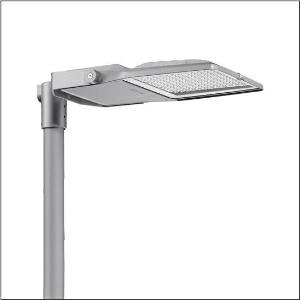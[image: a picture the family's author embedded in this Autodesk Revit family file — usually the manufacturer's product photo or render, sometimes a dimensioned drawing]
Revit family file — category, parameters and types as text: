
# Revit family: floodlight_fl_21_iq_midi___pl33t_5xa7782f4f3a_5715
name_source: partatom
category: Lighting Fixtures
units: mm (PartAtom-declared; Revit-internal decimal feet)

## family parameters
Cut with Voids When Loaded = No
Host = Face
Light Source = No
Part Type = Normal
Room Calculation Point = No
Round Connector Dimension = Use Diameter
Shared = No

## types (1)
- --- (1 x LED, 36900 lm, 270.2 W, 4000K)
    Apparent Load = 270 VA
    CIE Flux Codes = 26 75 99 100 100
    Color Rendering = 70
    Color Temperature = 4000K
    Default Elevation = 1800 mm
    Description = Floodlight FL 21 iQ midi, floodlight, primary light control with lens, of PMMA, primary optical cover: protective disc, of toughened safety glass, transparent, light distribution: PL33T, light emission: direct distribution, installation type: surface-mounted, LED, High Power LED, rated luminous flux: 36.900lm, luminous efficacy: 137lm/W, light colour: 740, colour temperature: 4000K, control gear: ECG iQ, control: optimised constant luminous flux control (CLO 2.0), Desk-Remote (wireless, voltage-free reading and setting of iQ features in the workshop via application-optimized NFC function/RFID function), Smart-Wire, Night-Set, Temp-Guard, Auto-Match, Street-Remote, with terminal, 6-pole, mains connection: 220..240V, AC, 50/60Hz, start of lifetime: 270W, end of service life: 287W, reduction: 118W, luminaire housing, of diecast aluminium, powder-coated, Siteco® metallic grey (DB 702S), corrosivity category C5 mid according to DIN EN ISO 12944, sealing non-destructively replaceable, please order mast flange separately, mast bracket, of steel, galvanised, powder-coated, Siteco® metallic grey (DB 702S), protection rating (complete): IP66, insulation class (complete): insulation class II (safety insulation), certification: CE, ENEC, VDE, protection symbol: D, impact resistance: IK08, permissible operating ambient temperature: -40..+40°C, permissible operating ambient temperature for outdoor applications: -40..+50°C, standard: DIN EN 12944, LABS conformity tested according to VDMA 24364:2018-05, packaging unit: 1 piece

Light Distribution: PL33T
    Height = 76 mm
    Lamp = 1 x LED
    Lamp Light Flux = 36900 lm
    Lamp Power = 270.2 W
    Lamp count = 1
    Length = 657 mm
    Luminous efficacy = 137 lm/W
    Manufacturer = Siteco
    ModVariant = No
    Model = 5XA7782F4F3A
    Number of Poles = 1
    OnlyDefault = Yes
    Power Factor = 1
    Product Name = Floodlight FL 21 iQ midi | PL33T
    Product group = floodlight | pylon annexe
    ProductGroupID = 6200
    Protection Class = Protection class II
    Protection Degree = IP 66
    RLX_Detail_Level = 1
    RLX_Emergency_Light_Flux = 0 lm
    RLX_Emergency_Type = 0
    RLX_Emergency_Type_DB = No
    RlxData = <blob elided: 153477 chars, md5=909a2a14>
    Socket = socket
    Standby Power = 0 W
    System Light Flux = 36900 lm
    System Power = 270 W
    Type Comments = factory setting: luminous flux: 100 % | dim-lin: 254 | 620 mA
    Type Image = l_1007123.jpg
    URL = http://relux.com
    VarID = @adj_072107
    Voltage = 0 V
    Weight = 0.00 kg
    Width = 442 mm

## geometry (parser evidence)
native form markers: Blend x4, Sweep x13
no freeform markers — native parametric forms only
